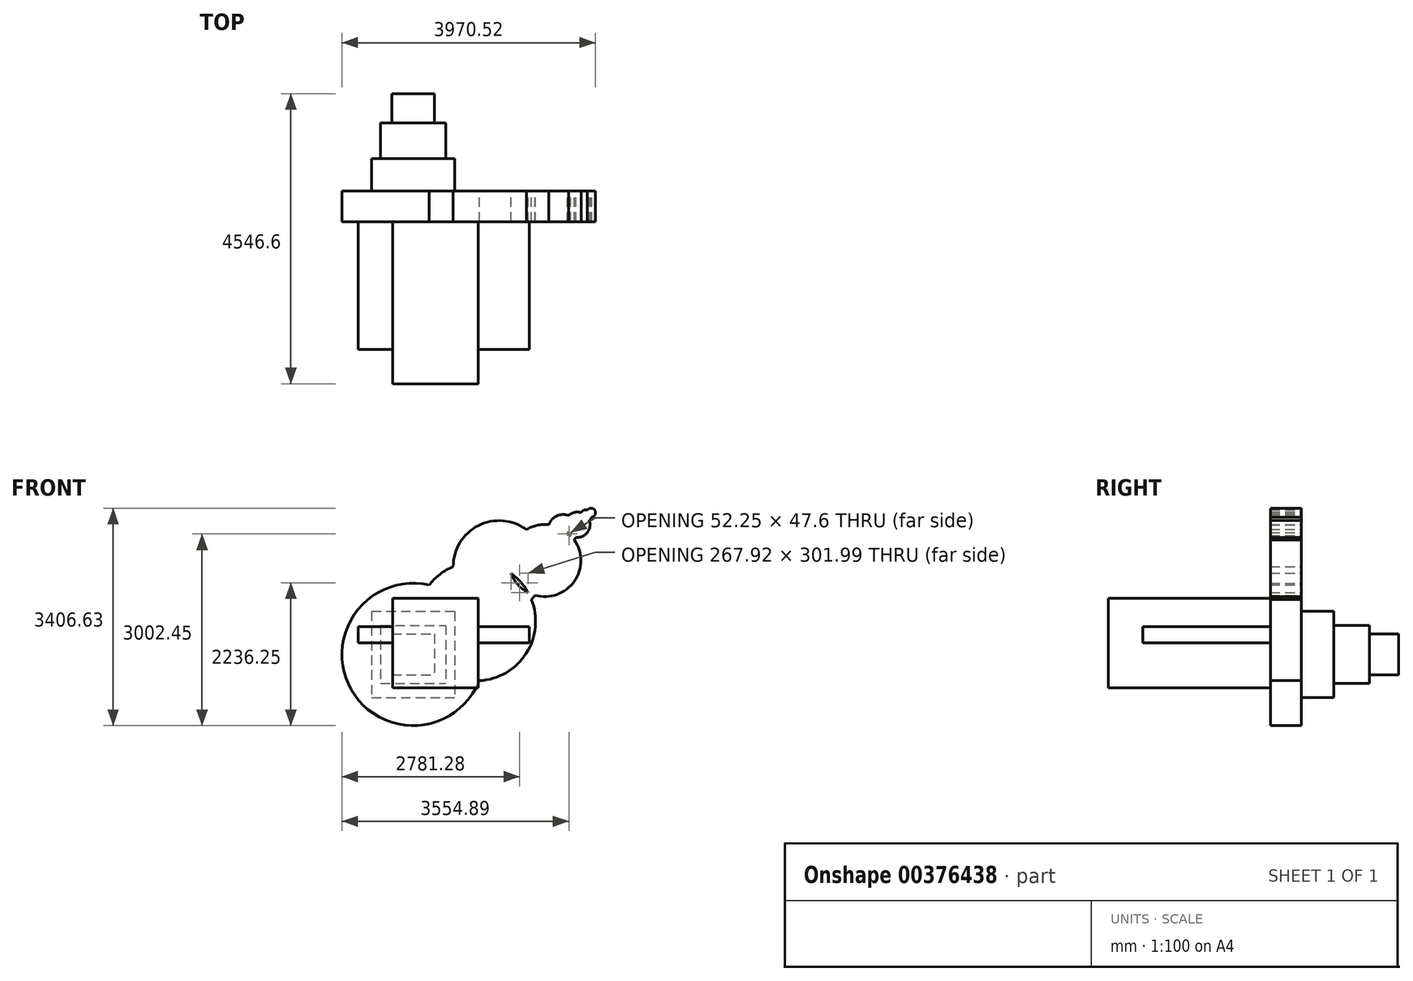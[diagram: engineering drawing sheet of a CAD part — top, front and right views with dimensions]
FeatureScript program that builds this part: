
annotation { "Feature Type Name" : "Feature", "Feature Type Description" : "" }
export const myFeature = defineFeature(function(context is Context, id is Id, definition is map)
    precondition{}
    {
        {
            var Q0;
            Q0=qCreatedBy(makeId("Front.planeOp"),FACE);
            var sketch = newSketch(context, id + "F0", { "sketchPlane" : qUnion([Q0])});
            skCircle(sketch, "E0", {"center": v(-70.27, 0.13) * mm, "radius": 70.27 * mm});
            skPoint(sketch, "E0.first.point", {"position": v(0, 0) * mm});
            skPoint(sketch, "E0.second.point", {"position": v(-59.88, 69.63) * mm});
            skPoint(sketch, "E0.third.point", {"position": v(-118.43, -51.04) * mm});
            skCircle(sketch, "E1", {"center": v(-147.64, -45.42) * mm, "radius": 89.78 * mm});
            skPoint(sketch, "E1.second.point", {"position": v(-126.77, 41.9) * mm});
            skPoint(sketch, "E1.third.point", {"position": v(-225.08, 0) * mm});
            skCircle(sketch, "E2", {"center": v(-284.14, -189.44) * mm, "radius": 198.43 * mm});
            skPoint(sketch, "E2.third.point", {"position": v(-420.64, -45.42) * mm});
            skCircle(sketch, "E3", {"center": v(-507.53, -264.47) * mm, "radius": 235.66 * mm});
            skPoint(sketch, "E3.third.point", {"position": v(-730.93, -189.44) * mm});
            skCircle(sketch, "E4", {"center": v(-794.97, -750.19) * mm, "radius": 564.4 * mm});
            skPoint(sketch, "E4.third.point", {"position": v(-1082.41, -264.47) * mm});
            skCircle(sketch, "E5", {"center": v(-1508.8, -844.71) * mm, "radius": 720.06 * mm});
            skPoint(sketch, "E5.third.point", {"position": v(-1935.2, -264.47) * mm});
            skCircle(sketch, "E6", {"center": v(-1868.83, -1702.9) * mm, "radius": 930.64 * mm});
            skPoint(sketch, "E6.second.point", {"position": v(-2228.86, -844.71) * mm});
            skPoint(sketch, "E6.third.point", {"position": v(-2606.06, -1134.92) * mm});
            skCircle(sketch, "E7", {"center": v(-2855.71, -2221.42) * mm, "radius": 1114.81 * mm});
            skPoint(sketch, "E7.third.point", {"position": v(-3968.12, -2148.17) * mm});
            skSolve(sketch);
        }
        {
            var Q0;
            Q0 = qSketchRegion(id + "F0", true);
            extrude(context, id + "F1", {"entities" : qUnion([Q0]), "depth" : 482.6 * mm});
        }
        {
            var Q0;
            Q0=makeQuery(id+"F1.opExtrude","CAP_FACE",FACE,{"disambiguationData":[OSD([sQuery(id+"F0.wireOp",EDGE,"E0"),sQuery(id+"F0.wireOp",EDGE,"E1"),sQuery(id+"F0.wireOp",EDGE,"E2"),sQuery(id+"F0.wireOp",EDGE,"E3"),sQuery(id+"F0.wireOp",EDGE,"E4"),sQuery(id+"F0.wireOp",EDGE,"E5"),sQuery(id+"F0.wireOp",EDGE,"E6"),sQuery(id+"F0.wireOp",EDGE,"E7")])],"isStart":false});
            var sketch = newSketch(context, id + "F2", { "sketchPlane" : qUnion([Q0])});
            skLineSegment(sketch, "E8.bottom", {"start": v(-3714.3, -2041.52) * mm, "end": v(-1038.54, -2041.52) * mm});
            skLineSegment(sketch, "E8.top", {"start": v(-3714.3, -1787.62) * mm, "end": v(-1038.54, -1787.62) * mm});
            skLineSegment(sketch, "E8.left", {"start": v(-3714.3, -2041.52) * mm, "end": v(-3714.3, -1787.62) * mm});
            skLineSegment(sketch, "E8.right", {"start": v(-1038.54, -2041.52) * mm, "end": v(-1038.54, -1787.62) * mm});
            skPoint(sketch, "E8.middle", {"position": v(-2376.42, -1914.57) * mm});
            skSolve(sketch);
        }
        {
            var Q0;
            Q0 = qSketchRegion(id + "F2", true);
            extrude(context, id + "F3", {"entities" : qUnion([Q0]), "operationType" : NewBodyOperationType.ADD, "depth" : 2000.8 * mm});
        }
        {
            var Q0;
            Q0=makeQuery(id+"F1.opExtrude","CAP_FACE",FACE,{"disambiguationData":[OSD([sQuery(id+"F0.wireOp",EDGE,"E0"),sQuery(id+"F0.wireOp",EDGE,"E1"),sQuery(id+"F0.wireOp",EDGE,"E2"),sQuery(id+"F0.wireOp",EDGE,"E3"),sQuery(id+"F0.wireOp",EDGE,"E4"),sQuery(id+"F0.wireOp",EDGE,"E5"),sQuery(id+"F0.wireOp",EDGE,"E6"),sQuery(id+"F0.wireOp",EDGE,"E7")])],"isStart":false});
            var sketch = newSketch(context, id + "F4", { "sketchPlane" : qUnion([Q0])});
            skLineSegment(sketch, "E9.bottom", {"start": v(-1836.2, -1338.45) * mm, "end": v(-3178.42, -1338.45) * mm});
            skLineSegment(sketch, "E9.top", {"start": v(-1836.2, -2744.59) * mm, "end": v(-3178.42, -2744.59) * mm});
            skLineSegment(sketch, "E9.left", {"start": v(-1836.2, -1338.45) * mm, "end": v(-1836.2, -2744.59) * mm});
            skLineSegment(sketch, "E9.right", {"start": v(-3178.42, -1338.45) * mm, "end": v(-3178.42, -2744.59) * mm});
            skPoint(sketch, "E9.middle", {"position": v(-2507.3, -2041.52) * mm});
            skSolve(sketch);
        }
        {
            var Q0;
            Q0 = qSketchRegion(id + "F4", true);
            extrude(context, id + "F5", {"entities" : qUnion([Q0]), "operationType" : NewBodyOperationType.ADD, "depth" : 2540 * mm});
        }
        {
            var Q0;
            Q0=makeQuery(id+"F1.opExtrude","CAP_FACE",FACE,{"disambiguationData":[OSD([sQuery(id+"F0.wireOp",EDGE,"E0"),sQuery(id+"F0.wireOp",EDGE,"E1"),sQuery(id+"F0.wireOp",EDGE,"E2"),sQuery(id+"F0.wireOp",EDGE,"E3"),sQuery(id+"F0.wireOp",EDGE,"E4"),sQuery(id+"F0.wireOp",EDGE,"E5"),sQuery(id+"F0.wireOp",EDGE,"E6"),sQuery(id+"F0.wireOp",EDGE,"E7")])],"isStart":true});
            var sketch = newSketch(context, id + "F6", { "sketchPlane" : qUnion([Q0])});
            skLineSegment(sketch, "E10.bottom", {"start": v(3505.33, -1547.5) * mm, "end": v(2206.1, -1547.5) * mm});
            skLineSegment(sketch, "E10.top", {"start": v(3505.33, -2895.33) * mm, "end": v(2206.1, -2895.33) * mm});
            skLineSegment(sketch, "E10.left", {"start": v(3505.33, -1547.5) * mm, "end": v(3505.33, -2895.33) * mm});
            skLineSegment(sketch, "E10.right", {"start": v(2206.1, -1547.5) * mm, "end": v(2206.1, -2895.33) * mm});
            skPoint(sketch, "E10.middle", {"position": v(2855.71, -2221.42) * mm});
            skLineSegment(sketch, "E11.bottom", {"start": v(3364.7, -1765.42) * mm, "end": v(2346.73, -1765.42) * mm});
            skLineSegment(sketch, "E11.top", {"start": v(3364.7, -2677.41) * mm, "end": v(2346.73, -2677.41) * mm});
            skLineSegment(sketch, "E11.left", {"start": v(3364.7, -1765.42) * mm, "end": v(3364.7, -2677.41) * mm});
            skLineSegment(sketch, "E11.right", {"start": v(2346.73, -1765.42) * mm, "end": v(2346.73, -2677.41) * mm});
            skLineSegment(sketch, "E12.bottom", {"start": v(3189.84, -1901.5) * mm, "end": v(2521.6, -1901.5) * mm});
            skLineSegment(sketch, "E12.top", {"start": v(3189.84, -2541.34) * mm, "end": v(2521.6, -2541.34) * mm});
            skLineSegment(sketch, "E12.left", {"start": v(3189.84, -1901.5) * mm, "end": v(3189.84, -2541.34) * mm});
            skLineSegment(sketch, "E12.right", {"start": v(2521.6, -1901.5) * mm, "end": v(2521.6, -2541.34) * mm});
            skSolve(sketch);
        }
        {
            var Q0;
            Q0=makeQuery(id+"F6.imprint","IMPRINT",FACE,{"disambiguationData":[TD([[makeQuery(id+"F6.imprint","IMPRINT",EDGE,{"derivedFrom":sQuery(id+"F6.wireOp",EDGE,"E12.bottom")}),1.0]])]});
            extrude(context, id + "F7", {"entities" : qUnion([Q0]), "operationType" : NewBodyOperationType.ADD, "depth" : 1524 * mm});
        }
        {
            var Q0;
            Q0=makeQuery(id+"F6.imprint","IMPRINT",FACE,{"disambiguationData":[TD([[makeQuery(id+"F6.imprint","IMPRINT",EDGE,{"derivedFrom":sQuery(id+"F6.wireOp",EDGE,"E11.bottom")}),1.0]])]});
            extrude(context, id + "F8", {"entities" : qUnion([Q0]), "operationType" : NewBodyOperationType.ADD, "depth" : 1066.8 * mm});
        }
        {
            var Q0;
            Q0=makeQuery(id+"F6.imprint","IMPRINT",FACE,{"disambiguationData":[TD([[makeQuery(id+"F6.imprint","IMPRINT",EDGE,{"derivedFrom":sQuery(id+"F6.wireOp",EDGE,"E10.bottom")}),1.0]])]});
            extrude(context, id + "F9", {"entities" : qUnion([Q0]), "operationType" : NewBodyOperationType.ADD, "depth" : 508 * mm});
        }
    });
